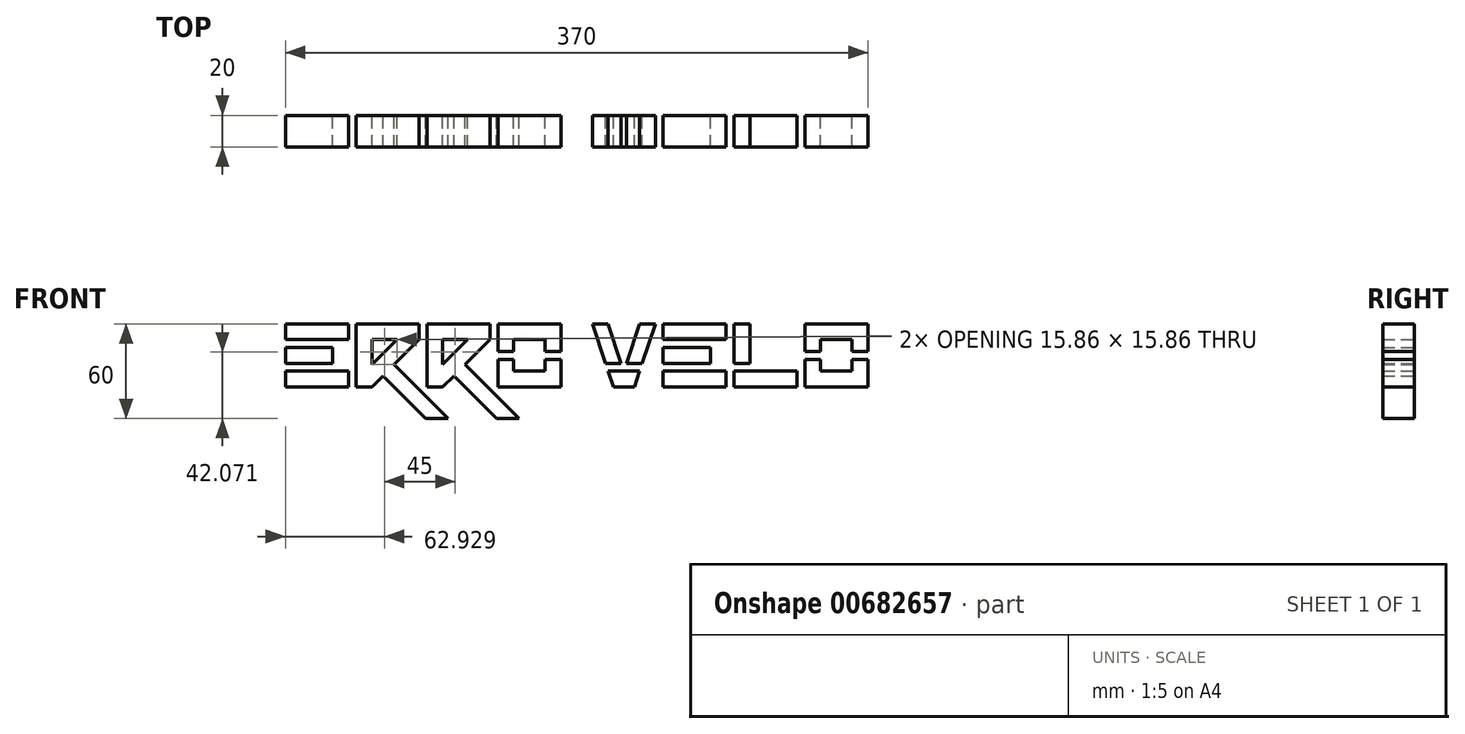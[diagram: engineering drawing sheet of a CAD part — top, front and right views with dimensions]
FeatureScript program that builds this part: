
annotation { "Feature Type Name" : "Feature", "Feature Type Description" : "" }
export const myFeature = defineFeature(function(context is Context, id is Id, definition is map)
    precondition{}
    {
        {
            var Q0;
            Q0=qCreatedBy(makeId("Front.planeOp"),FACE);
            var sketch = newSketch(context, id + "F0", { "sketchPlane" : qUnion([Q0])});
            skLineSegment(sketch, "E0.bottom", {"start": v(0, 0) * mm, "end": v(-40, 0) * mm});
            skLineSegment(sketch, "E0.top", {"start": v(0, 10) * mm, "end": v(-40, 10) * mm});
            skLineSegment(sketch, "E0.left", {"start": v(0, 0) * mm, "end": v(0, 10) * mm});
            skLineSegment(sketch, "E0.right", {"start": v(-40, 0) * mm, "end": v(-40, 10) * mm});
            skLineSegment(sketch, "E1.bottom", {"start": v(-40, 25) * mm, "end": v(-10, 25) * mm});
            skLineSegment(sketch, "E1.top", {"start": v(-40, 15) * mm, "end": v(-10, 15) * mm});
            skLineSegment(sketch, "E1.left", {"start": v(-40, 25) * mm, "end": v(-40, 15) * mm});
            skLineSegment(sketch, "E1.right", {"start": v(-10, 25) * mm, "end": v(-10, 15) * mm});
            skLineSegment(sketch, "E2.bottom", {"start": v(-40, 30) * mm, "end": v(0, 30) * mm});
            skLineSegment(sketch, "E2.top", {"start": v(-40, 40) * mm, "end": v(0, 40) * mm});
            skLineSegment(sketch, "E2.left", {"start": v(-40, 30) * mm, "end": v(-40, 40) * mm});
            skLineSegment(sketch, "E2.right", {"start": v(0, 30) * mm, "end": v(0, 40) * mm});
            skLineSegment(sketch, "E3", {"start": v(5, 0) * mm, "end": v(5, 40) * mm});
            skLineSegment(sketch, "E4", {"start": v(5, 40) * mm, "end": v(45, 40) * mm});
            skLineSegment(sketch, "E5", {"start": v(45, 40) * mm, "end": v(45, 30) * mm});
            skLineSegment(sketch, "E6", {"start": v(15, 0) * mm, "end": v(5, 0) * mm});
            skLineSegment(sketch, "E7", {"start": v(45, 30) * mm, "end": v(29.14, 14.14) * mm});
            skLineSegment(sketch, "E8", {"start": v(15, 0) * mm, "end": v(15, 0) * mm});
            skLineSegment(sketch, "E9", {"start": v(15, 30) * mm, "end": v(30.86, 30) * mm});
            skLineSegment(sketch, "E10", {"start": v(30.86, 30) * mm, "end": v(15, 14.14) * mm});
            skLineSegment(sketch, "E11", {"start": v(15, 14.14) * mm, "end": v(15, 30) * mm});
            skLineSegment(sketch, "E12", {"start": v(22.07, 7.07) * mm, "end": v(49.14, -20) * mm});
            skLineSegment(sketch, "E13", {"start": v(49.14, -20) * mm, "end": v(63.28, -20) * mm});
            skLineSegment(sketch, "E14", {"start": v(63.28, -20) * mm, "end": v(29.14, 14.14) * mm});
            skLineSegment(sketch, "E15", {"start": v(15, 14.14) * mm, "end": v(22.07, 7.07) * mm, "construction": true});
            skLineSegment(sketch, "E16.trimOffspring", {"start": v(22.07, 7.07) * mm, "end": v(15, 0) * mm});
            skLineSegment(sketch, "E17", {"start": v(50, 0) * mm, "end": v(50, 40) * mm});
            skLineSegment(sketch, "E18", {"start": v(50, 40) * mm, "end": v(90, 40) * mm});
            skLineSegment(sketch, "E19", {"start": v(90, 40) * mm, "end": v(90, 30) * mm});
            skLineSegment(sketch, "E20", {"start": v(60, 0) * mm, "end": v(50, 0) * mm});
            skLineSegment(sketch, "E21", {"start": v(90, 30) * mm, "end": v(74.14, 14.14) * mm});
            skLineSegment(sketch, "E22", {"start": v(60, 30) * mm, "end": v(75.86, 30) * mm});
            skLineSegment(sketch, "E23", {"start": v(75.86, 30) * mm, "end": v(60, 14.14) * mm});
            skLineSegment(sketch, "E24", {"start": v(60, 14.14) * mm, "end": v(60, 30) * mm});
            skLineSegment(sketch, "E25", {"start": v(67.07, 7.07) * mm, "end": v(94.14, -20) * mm});
            skLineSegment(sketch, "E26", {"start": v(94.14, -20) * mm, "end": v(108.28, -20) * mm});
            skLineSegment(sketch, "E27", {"start": v(108.28, -20) * mm, "end": v(74.14, 14.14) * mm});
            skLineSegment(sketch, "E28", {"start": v(60, 14.14) * mm, "end": v(67.07, 7.07) * mm, "construction": true});
            skLineSegment(sketch, "E29.trimOffspring", {"start": v(67.07, 7.07) * mm, "end": v(60, 0) * mm});
            skLineSegment(sketch, "E30.bottom", {"start": v(95, 0) * mm, "end": v(135, 0) * mm});
            skLineSegment(sketch, "E30.top", {"start": v(95, 40) * mm, "end": v(135, 40) * mm});
            skLineSegment(sketch, "E30.left", {"start": v(95, 0) * mm, "end": v(95, 17.5) * mm});
            skLineSegment(sketch, "E30.right", {"start": v(135, 0) * mm, "end": v(135, 17.5) * mm});
            skLineSegment(sketch, "E31.bottom", {"start": v(105, 30) * mm, "end": v(125, 30) * mm});
            skLineSegment(sketch, "E31.top", {"start": v(105, 10) * mm, "end": v(125, 10) * mm});
            skLineSegment(sketch, "E31.left", {"start": v(105, 30) * mm, "end": v(105, 22.5) * mm});
            skLineSegment(sketch, "E31.right", {"start": v(125, 30) * mm, "end": v(125, 22.5) * mm});
            skLineSegment(sketch, "E32", {"start": v(95, 17.5) * mm, "end": v(105, 17.5) * mm});
            skLineSegment(sketch, "E33", {"start": v(105, 22.5) * mm, "end": v(95, 22.5) * mm});
            skLineSegment(sketch, "E34", {"start": v(125, 22.5) * mm, "end": v(135, 22.5) * mm});
            skLineSegment(sketch, "E35", {"start": v(125, 17.5) * mm, "end": v(135, 17.5) * mm});
            skLineSegment(sketch, "E36.trimOffspring", {"start": v(95, 22.5) * mm, "end": v(95, 40) * mm});
            skLineSegment(sketch, "E37.trimOffspring", {"start": v(105, 17.5) * mm, "end": v(105, 10) * mm});
            skLineSegment(sketch, "E38.trimOffspring", {"start": v(125, 17.5) * mm, "end": v(125, 10) * mm});
            skLineSegment(sketch, "E39.trimOffspring", {"start": v(135, 22.5) * mm, "end": v(135, 40) * mm});
            skLineSegment(sketch, "E40", {"start": v(155, 40) * mm, "end": v(163.33, 15) * mm});
            skLineSegment(sketch, "E41", {"start": v(168.33, 0) * mm, "end": v(181.67, 0) * mm});
            skLineSegment(sketch, "E42", {"start": v(181.67, 0) * mm, "end": v(185, 10) * mm});
            skLineSegment(sketch, "E43", {"start": v(195, 40) * mm, "end": v(185, 40) * mm});
            skLineSegment(sketch, "E44", {"start": v(185, 40) * mm, "end": v(176.67, 15) * mm});
            skLineSegment(sketch, "E45", {"start": v(173.33, 15) * mm, "end": v(165, 40) * mm});
            skLineSegment(sketch, "E46", {"start": v(165, 40) * mm, "end": v(155, 40) * mm});
            skLineSegment(sketch, "E47.bottom", {"start": v(240, 0) * mm, "end": v(200, 0) * mm});
            skLineSegment(sketch, "E47.top", {"start": v(240, 10) * mm, "end": v(200, 10) * mm});
            skLineSegment(sketch, "E47.left", {"start": v(240, 0) * mm, "end": v(240, 10) * mm});
            skLineSegment(sketch, "E47.right", {"start": v(200, 0) * mm, "end": v(200, 10) * mm});
            skLineSegment(sketch, "E48.bottom", {"start": v(200, 25) * mm, "end": v(230, 25) * mm});
            skLineSegment(sketch, "E48.top", {"start": v(200, 15) * mm, "end": v(230, 15) * mm});
            skLineSegment(sketch, "E48.left", {"start": v(200, 25) * mm, "end": v(200, 15) * mm});
            skLineSegment(sketch, "E48.right", {"start": v(230, 25) * mm, "end": v(230, 15) * mm});
            skLineSegment(sketch, "E49.bottom", {"start": v(200, 30) * mm, "end": v(240, 30) * mm});
            skLineSegment(sketch, "E49.top", {"start": v(200, 40) * mm, "end": v(240, 40) * mm});
            skLineSegment(sketch, "E49.left", {"start": v(200, 30) * mm, "end": v(200, 40) * mm});
            skLineSegment(sketch, "E49.right", {"start": v(240, 30) * mm, "end": v(240, 40) * mm});
            skLineSegment(sketch, "E50", {"start": v(245, 40) * mm, "end": v(245, 15) * mm});
            skLineSegment(sketch, "E51", {"start": v(245, 0) * mm, "end": v(285, 0) * mm});
            skLineSegment(sketch, "E52", {"start": v(285, 0) * mm, "end": v(285, 10) * mm});
            skLineSegment(sketch, "E53", {"start": v(285, 10) * mm, "end": v(255, 10) * mm});
            skLineSegment(sketch, "E54", {"start": v(255, 15) * mm, "end": v(255, 40) * mm});
            skLineSegment(sketch, "E55", {"start": v(255, 40) * mm, "end": v(245, 40) * mm});
            skLineSegment(sketch, "E56.bottom", {"start": v(290, 0) * mm, "end": v(330, 0) * mm});
            skLineSegment(sketch, "E56.top", {"start": v(290, 40) * mm, "end": v(330, 40) * mm});
            skLineSegment(sketch, "E56.left", {"start": v(290, 0) * mm, "end": v(290, 17.5) * mm});
            skLineSegment(sketch, "E56.right", {"start": v(330, 0) * mm, "end": v(330, 17.5) * mm});
            skLineSegment(sketch, "E57.bottom", {"start": v(300, 30) * mm, "end": v(320, 30) * mm});
            skLineSegment(sketch, "E57.top", {"start": v(300, 10) * mm, "end": v(320, 10) * mm});
            skLineSegment(sketch, "E57.left", {"start": v(300, 30) * mm, "end": v(300, 22.5) * mm});
            skLineSegment(sketch, "E57.right", {"start": v(320, 30) * mm, "end": v(320, 22.5) * mm});
            skLineSegment(sketch, "E58", {"start": v(290, 17.5) * mm, "end": v(300, 17.5) * mm});
            skLineSegment(sketch, "E59", {"start": v(300, 22.5) * mm, "end": v(290, 22.5) * mm});
            skLineSegment(sketch, "E60", {"start": v(320, 22.5) * mm, "end": v(330, 22.5) * mm});
            skLineSegment(sketch, "E61", {"start": v(320, 17.5) * mm, "end": v(330, 17.5) * mm});
            skLineSegment(sketch, "E62.trimOffspring", {"start": v(290, 22.5) * mm, "end": v(290, 40) * mm});
            skLineSegment(sketch, "E63.trimOffspring", {"start": v(300, 17.5) * mm, "end": v(300, 10) * mm});
            skLineSegment(sketch, "E64.trimOffspring", {"start": v(320, 17.5) * mm, "end": v(320, 10) * mm});
            skLineSegment(sketch, "E65.trimOffspring", {"start": v(330, 22.5) * mm, "end": v(330, 40) * mm});
            skLineSegment(sketch, "E66", {"start": v(185, 10) * mm, "end": v(165, 10) * mm});
            skLineSegment(sketch, "E67", {"start": v(163.33, 15) * mm, "end": v(173.33, 15) * mm});
            skLineSegment(sketch, "E68.trimOffspring", {"start": v(176.67, 15) * mm, "end": v(186.67, 15) * mm});
            skLineSegment(sketch, "E69.trimOffspring", {"start": v(165, 10) * mm, "end": v(168.33, 0) * mm});
            skLineSegment(sketch, "E70.trimOffspring", {"start": v(186.67, 15) * mm, "end": v(195, 40) * mm});
            skPoint(sketch, "E71.orphan", {"position": v(175, 10) * mm});
            skLineSegment(sketch, "E72", {"start": v(255, 10) * mm, "end": v(245, 10) * mm});
            skLineSegment(sketch, "E73", {"start": v(245, 15) * mm, "end": v(255, 15) * mm});
            skLineSegment(sketch, "E74.trimOffspring", {"start": v(245, 10) * mm, "end": v(245, 0) * mm});
            skSolve(sketch);
        }
        {
            var Q0;
            Q0=makeQuery(id+"F0.imprint","IMPRINT",FACE,{"disambiguationData":[TD([[makeQuery(id+"F0.imprint","IMPRINT",EDGE,{"derivedFrom":sQuery(id+"F0.wireOp",EDGE,"E2.bottom")}),1.0]])]});
            var Q1;
            Q1=makeQuery(id+"F0.imprint","IMPRINT",FACE,{"disambiguationData":[TD([[makeQuery(id+"F0.imprint","IMPRINT",EDGE,{"derivedFrom":sQuery(id+"F0.wireOp",EDGE,"E1.bottom")}),-1.0]])]});
            var Q2;
            Q2=makeQuery(id+"F0.imprint","IMPRINT",FACE,{"disambiguationData":[TD([[makeQuery(id+"F0.imprint","IMPRINT",EDGE,{"derivedFrom":sQuery(id+"F0.wireOp",EDGE,"E0.bottom")}),-1.0]])]});
            var Q3;
            Q3=makeQuery(id+"F0.imprint","IMPRINT",FACE,{"disambiguationData":[TD([[makeQuery(id+"F0.imprint","IMPRINT",EDGE,{"derivedFrom":sQuery(id+"F0.wireOp",EDGE,"E3")}),-1.0]])]});
            var Q4;
            Q4=makeQuery(id+"F0.imprint","IMPRINT",FACE,{"disambiguationData":[TD([[makeQuery(id+"F0.imprint","IMPRINT",EDGE,{"derivedFrom":sQuery(id+"F0.wireOp",EDGE,"E17")}),-1.0]])]});
            var Q5;
            Q5=makeQuery(id+"F0.imprint","IMPRINT",FACE,{"disambiguationData":[TD([[makeQuery(id+"F0.imprint","IMPRINT",EDGE,{"derivedFrom":sQuery(id+"F0.wireOp",EDGE,"E30.top")}),-1.0]])]});
            var Q6;
            Q6=makeQuery(id+"F0.imprint","IMPRINT",FACE,{"disambiguationData":[TD([[makeQuery(id+"F0.imprint","IMPRINT",EDGE,{"derivedFrom":sQuery(id+"F0.wireOp",EDGE,"E30.bottom")}),1.0]])]});
            var Q7;
            Q7=makeQuery(id+"F0.imprint","IMPRINT",FACE,{"disambiguationData":[TD([[makeQuery(id+"F0.imprint","IMPRINT",EDGE,{"derivedFrom":sQuery(id+"F0.wireOp",EDGE,"E40")}),1.0]])]});
            var Q8;
            Q8=makeQuery(id+"F0.imprint","IMPRINT",FACE,{"disambiguationData":[TD([[makeQuery(id+"F0.imprint","IMPRINT",EDGE,{"derivedFrom":sQuery(id+"F0.wireOp",EDGE,"E49.bottom")}),1.0]])]});
            var Q9;
            Q9=makeQuery(id+"F0.imprint","IMPRINT",FACE,{"disambiguationData":[TD([[makeQuery(id+"F0.imprint","IMPRINT",EDGE,{"derivedFrom":sQuery(id+"F0.wireOp",EDGE,"E48.bottom")}),-1.0]])]});
            var Q10;
            Q10=makeQuery(id+"F0.imprint","IMPRINT",FACE,{"disambiguationData":[TD([[makeQuery(id+"F0.imprint","IMPRINT",EDGE,{"derivedFrom":sQuery(id+"F0.wireOp",EDGE,"E47.bottom")}),-1.0]])]});
            var Q11;
            Q11=makeQuery(id+"F0.imprint","IMPRINT",FACE,{"disambiguationData":[TD([[makeQuery(id+"F0.imprint","IMPRINT",EDGE,{"derivedFrom":sQuery(id+"F0.wireOp",EDGE,"E50")}),1.0]])]});
            var Q12;
            Q12=makeQuery(id+"F0.imprint","IMPRINT",FACE,{"disambiguationData":[TD([[makeQuery(id+"F0.imprint","IMPRINT",EDGE,{"derivedFrom":sQuery(id+"F0.wireOp",EDGE,"E56.top")}),-1.0]])]});
            var Q13;
            Q13=makeQuery(id+"F0.imprint","IMPRINT",FACE,{"disambiguationData":[TD([[makeQuery(id+"F0.imprint","IMPRINT",EDGE,{"derivedFrom":sQuery(id+"F0.wireOp",EDGE,"E56.bottom")}),1.0]])]});
            var Q14;
            Q14=makeQuery(id+"F0.imprint","IMPRINT",FACE,{"disambiguationData":[TD([[makeQuery(id+"F0.imprint","IMPRINT",EDGE,{"derivedFrom":sQuery(id+"F0.wireOp",EDGE,"E43")}),1.0]])]});
            var Q15;
            Q15=makeQuery(id+"F0.imprint","IMPRINT",FACE,{"disambiguationData":[TD([[makeQuery(id+"F0.imprint","IMPRINT",EDGE,{"derivedFrom":sQuery(id+"F0.wireOp",EDGE,"E41")}),1.0]])]});
            var Q16;
            Q16=makeQuery(id+"F0.imprint","IMPRINT",FACE,{"disambiguationData":[TD([[makeQuery(id+"F0.imprint","IMPRINT",EDGE,{"derivedFrom":sQuery(id+"F0.wireOp",EDGE,"E51")}),1.0]])]});
            extrude(context, id + "F1", {"entities" : qUnion([Q0, Q1, Q2, Q3, Q4, Q5, Q6, Q7, Q8, Q9, Q10, Q11, Q12, Q13, Q14, Q15, Q16]), "depth" : 20 * mm, "offsetDistance" : 25 * mm});
        }
    });
